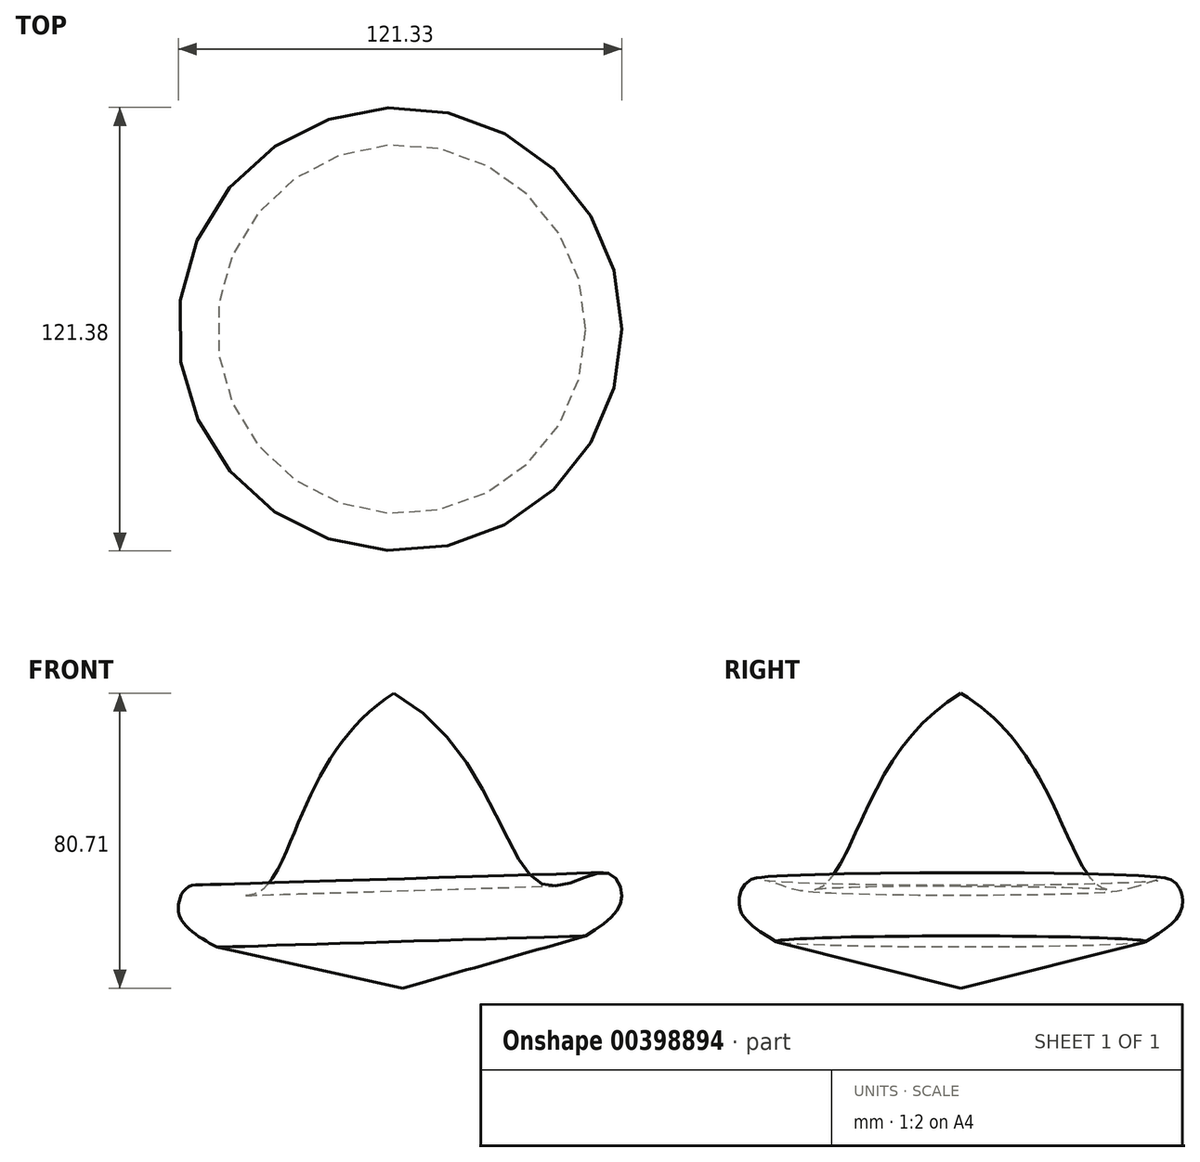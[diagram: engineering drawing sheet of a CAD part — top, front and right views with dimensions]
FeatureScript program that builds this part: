
annotation { "Feature Type Name" : "Feature", "Feature Type Description" : "" }
export const myFeature = defineFeature(function(context is Context, id is Id, definition is map)
    precondition{}
    {
        {
            var Q0;
            Q0=qCreatedBy(makeId("Front.planeOp"),FACE);
            var sketch = newSketch(context, id + "F0", { "sketchPlane" : qUnion([Q0])});
            skLineSegment(sketch, "E0", {"start": v(-52.52, 43.35) * mm, "end": v(-50.05, -37.36) * mm});
            skLineSegment(sketch, "E1", {"start": v(-50.05, -37.36) * mm, "end": v(0, -23.07) * mm});
            skFitSpline(sketch, "E2", {"points": [v(0, -23.07) * mm, v(7.75, -17.15) * mm, v(9.87, -11.6) * mm, v(5.64, -5.77) * mm, v(-11.63, -9) * mm, v(-52.52, 43.35) * mm], "startDerivative": vector(58.52, 36.52) * mm, "endDerivative": vector(-202.38, 111.48) * mm});
            skSolve(sketch);
        }
        {
            var Q0;
            Q0=makeQuery(id+"F0.imprint","IMPRINT",FACE,{"disambiguationData":[TD([[makeQuery(id+"F0.imprint","IMPRINT",EDGE,{"derivedFrom":sQuery(id+"F0.wireOp",EDGE,"E0")}),1.0]])]});
            var Q1;
            Q1=sQuery(id+"F0.wireOp",EDGE,"E0");
            revolve(context, id + "F1", {"entities" : qUnion([Q0]), "axis" : qUnion([Q1]), "revolveType" : RevolveType.FULL});
        }
    });
